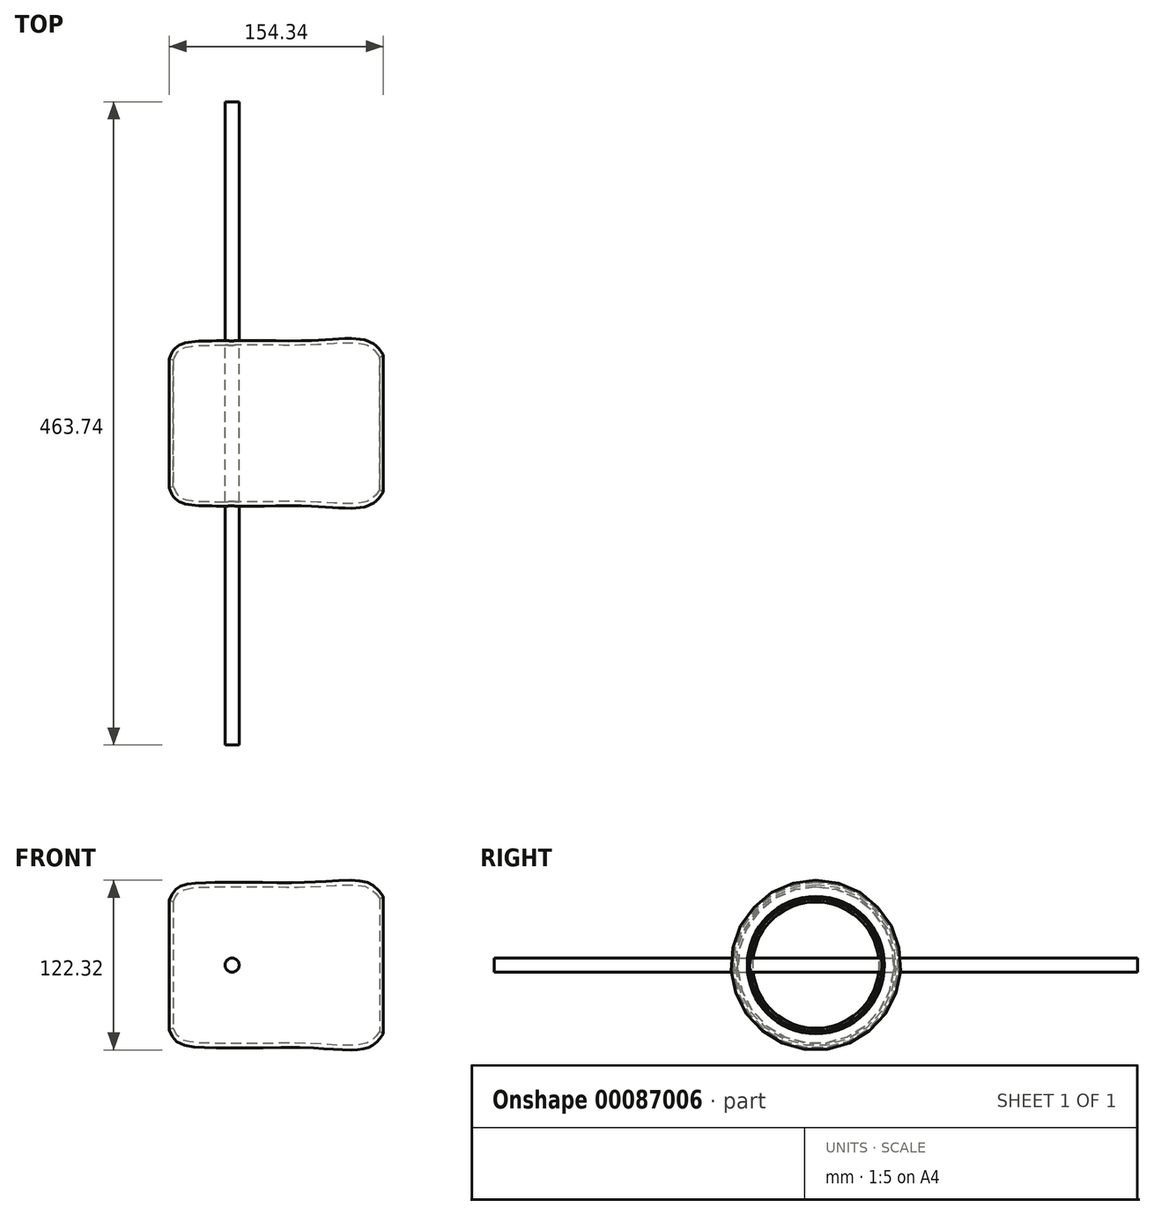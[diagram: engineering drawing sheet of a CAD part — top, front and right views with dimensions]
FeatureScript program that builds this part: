
annotation { "Feature Type Name" : "Feature", "Feature Type Description" : "" }
export const myFeature = defineFeature(function(context is Context, id is Id, definition is map)
    precondition{}
    {
        {
            var Q0;
            Q0=qCreatedBy(makeId("Top.planeOp"),FACE);
            var sketch = newSketch(context, id + "F0", { "sketchPlane" : qUnion([Q0])});
            skCircle(sketch, "E0", {"center": v(-25.27, 29.7) * mm, "radius": 20.73 * mm});
            skSolve(sketch);
        }
        {
            var Q0;
            Q0=qCreatedBy(makeId("Top.planeOp"),FACE);
            var sketch = newSketch(context, id + "F1", { "sketchPlane" : qUnion([Q0])});
            skFitSpline(sketch, "E1", {"points": [v(-71.27, 45.51) * mm, v(-66.24, 53.18) * mm, v(-45.87, 56.3) * mm, v(-10.66, 56.53) * mm, v(32.94, 56.77) * mm, v(68.15, 56.3) * mm, v(77.5, 47.67) * mm], "startDerivative": vector(33.13, 85.8) * mm, "endDerivative": vector(58.8, -85.52) * mm});
            skFitSpline(sketch, "E2.0", {"points": [v(-74.23, 46.66) * mm, v(-73.88, 47.55) * mm, v(-73.34, 48.98) * mm, v(-72.37, 50.95) * mm, v(-71.47, 52.44) * mm, v(-70.33, 53.89) * mm, v(-69.16, 55) * mm, v(-68.2, 55.7) * mm, v(-67.62, 56.06) * mm, v(-66.74, 56.58) * mm, v(-65.34, 57.22) * mm, v(-63.35, 57.87) * mm, v(-61.25, 58.37) * mm, v(-59.05, 58.73) * mm, v(-55.98, 59.08) * mm, v(-51.94, 59.33) * mm, v(-47.71, 59.43) * mm, v(-44.3, 59.5) * mm, v(-40.83, 59.57) * mm, v(-36.42, 59.64) * mm, v(-31, 59.7) * mm, v(-25.47, 59.74) * mm, v(-19.84, 59.76) * mm, v(-14.1, 59.74) * mm, v(-8.26, 59.69) * mm, v(-0.38, 59.58) * mm, v(7.65, 59.48) * mm, v(15.8, 59.47) * mm, v(21.97, 59.54) * mm, v(27.15, 59.69) * mm, v(31.32, 59.86) * mm, v(35.5, 60.1) * mm, v(40.79, 60.45) * mm, v(47.05, 60.86) * mm, v(53.1, 61.13) * mm, v(57.84, 61.12) * mm, v(61.4, 60.9) * mm, v(63.96, 60.61) * mm, v(66.38, 60.17) * mm, v(68.29, 59.64) * mm, v(69.74, 59.1) * mm, v(71.11, 58.48) * mm, v(72.68, 57.59) * mm, v(74.34, 56.36) * mm, v(76.27, 54.59) * mm, v(78.22, 52.22) * mm, v(79.5, 50.36) * mm, v(80.11, 49.47) * mm]});
            skLineSegment(sketch, "E3", {"start": v(-74.23, 46.66) * mm, "end": v(-71.27, 45.51) * mm});
            skLineSegment(sketch, "E4", {"start": v(80.11, 49.47) * mm, "end": v(77.5, 47.67) * mm});
            skLineSegment(sketch, "E5", {"start": v(-66, 0) * mm, "end": v(70.55, 0) * mm});
            skLineSegment(sketch, "E6", {"start": v(70.55, 0) * mm, "end": v(70.55, 0.72) * mm});
            skSolve(sketch);
        }
        {
            var Q0;
            Q0=makeQuery(id+"F1.imprint","IMPRINT",FACE,{"disambiguationData":[TD([[makeQuery(id+"F1.imprint","IMPRINT",EDGE,{"derivedFrom":sQuery(id+"F1.wireOp",EDGE,"E1")}),1.0]])]});
            var Q1;
            Q1=sQuery(id+"F1.wireOp",EDGE,"E5");
            revolve(context, id + "F2", {"entities" : qUnion([Q0]), "axis" : qUnion([Q1]), "revolveType" : RevolveType.FULL});
        }
        {
            var Q0;
            Q0=qCreatedBy(makeId("Front.planeOp"),FACE);
            var sketch = newSketch(context, id + "F3", { "sketchPlane" : qUnion([Q0])});
            skCircle(sketch, "E7", {"center": v(-28.95, 0) * mm, "radius": 5.1 * mm});
            skCircle(sketch, "E8", {"center": v(39.33, 0) * mm, "radius": 4.42 * mm});
            skSolve(sketch);
        }
        {
            var Q0;
            Q0=makeQuery(id+"F3.imprint","IMPRINT",FACE,{"disambiguationData":[TD([[makeQuery(id+"F3.imprint","IMPRINT",EDGE,{"derivedFrom":sQuery(id+"F3.wireOp",EDGE,"E7")}),1.0]])]});
            extrude(context, id + "F4", {"entities" : qUnion([Q0]), "operationType" : NewBodyOperationType.ADD, "endBound" : BoundingType.THROUGH_ALL, "depth" : 158.3 * mm, "hasSecondDirection" : true, "secondDirectionBound" : SecondDirectionBoundingType.THROUGH_ALL, "secondDirectionOppositeDirection" : true, "secondDirectionDepth" : 25.4 * mm});
        }
    });
